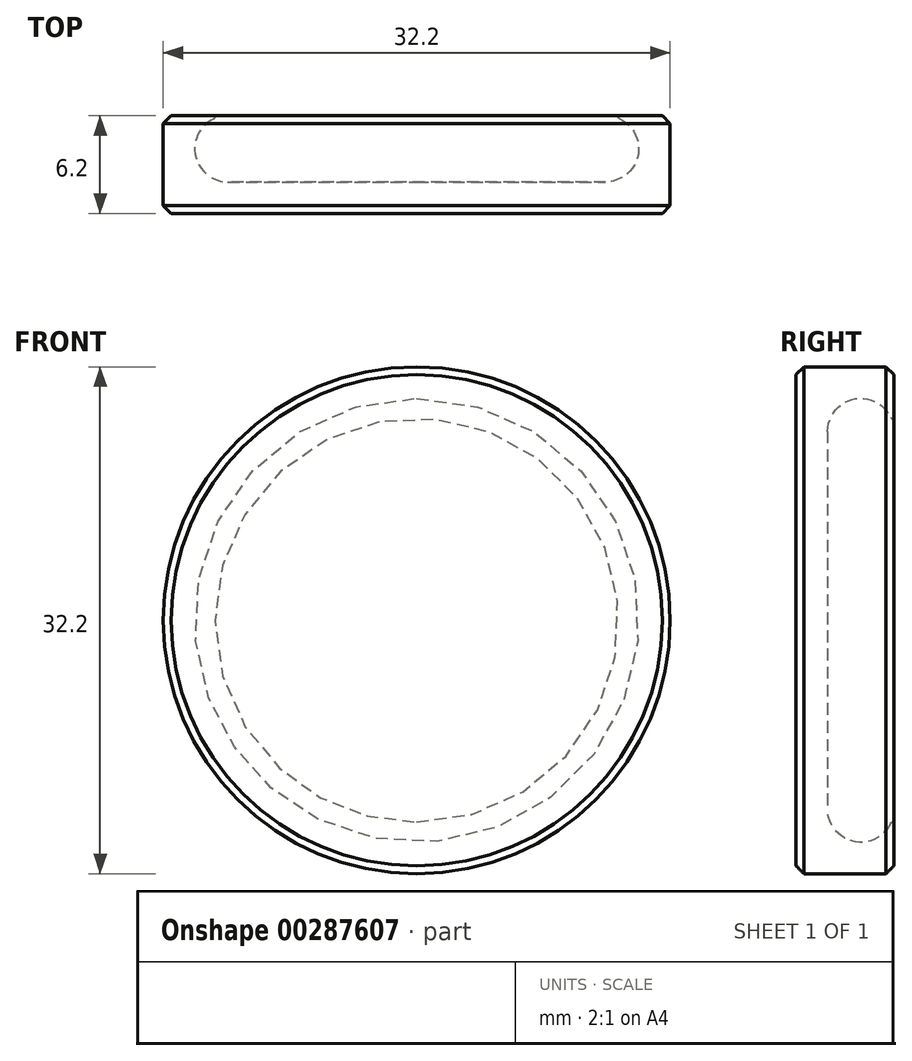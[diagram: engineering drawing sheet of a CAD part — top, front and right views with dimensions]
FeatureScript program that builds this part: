
annotation { "Feature Type Name" : "Feature", "Feature Type Description" : "" }
export const myFeature = defineFeature(function(context is Context, id is Id, definition is map)
    precondition{}
    {
        {
            var Q0;
            Q0=qCreatedBy(makeId("Top.planeOp"),FACE);
            var sketch = newSketch(context, id + "F0", { "sketchPlane" : qUnion([Q0])});
            skLineSegment(sketch, "E0", {"start": v(0, 0) * mm, "end": v(12, 0) * mm, "construction": true});
            skCircle(sketch, "E1", {"center": v(12, 0) * mm, "radius": 2.1 * mm});
            skLineSegment(sketch, "E2", {"start": v(12, -2.1) * mm, "end": v(0, -2.1) * mm});
            skLineSegment(sketch, "E3", {"start": v(14.1, 0) * mm, "end": v(14.1, 2.1) * mm});
            skLineSegment(sketch, "E4", {"start": v(14.1, 2.1) * mm, "end": v(12, 2.1) * mm});
            skLineSegment(sketch, "E5", {"start": v(12, -2.1) * mm, "end": v(16.1, -2.1) * mm});
            skLineSegment(sketch, "E6", {"start": v(16.1, -2.1) * mm, "end": v(16.1, 2.1) * mm});
            skLineSegment(sketch, "E7", {"start": v(16.1, 2.1) * mm, "end": v(14.1, 2.1) * mm});
            skLineSegment(sketch, "E8", {"start": v(16.1, -4.1) * mm, "end": v(0, -4.1) * mm});
            skLineSegment(sketch, "E9", {"start": v(16.1, -4.1) * mm, "end": v(16.1, -2.1) * mm});
            skLineSegment(sketch, "E10", {"start": v(0, -2.1) * mm, "end": v(0, -4.1) * mm});
            skSolve(sketch);
        }
        {
            var Q0;
            Q0=qCreatedBy(makeId("Right.planeOp"),FACE);
            var sketch = newSketch(context, id + "F1", { "sketchPlane" : qUnion([Q0])});
            skLineSegment(sketch, "E11", {"start": v(7.83, 0) * mm, "end": v(-14.6, 0) * mm, "construction": true});
            skSolve(sketch);
        }
        {
            var Q0;
            Q0=makeQuery(id+"F0.imprint","IMPRINT",FACE,{"disambiguationData":[TD([[makeQuery(id+"F0.imprint","IMPRINT",EDGE,{"derivedFrom":sQuery(id+"F0.wireOp",EDGE,"E2")}),1.0]])]});
            var Q1;
            {var subQ1=sQuery(id+"F0.wireOp",EDGE,"E3");Q1=makeQuery(id+"F0.imprint","IMPRINT",FACE,{"disambiguationData":[TD([[makeQuery(id+"F0.imprint","IMPRINT",EDGE,{"derivedFrom":subQ1}),-1.0]])]});}
            var Q2;
            {var subQ0=sQuery(id+"F0.wireOp",EDGE,"E3");Q2=makeQuery(id+"F0.imprint","IMPRINT",FACE,{"disambiguationData":[TD([[makeQuery(id+"F0.imprint","IMPRINT",EDGE,{"derivedFrom":subQ0}),1.0]])]});}
            var Q3;
            Q3=sQuery(id+"F1.wireOp",EDGE,"E11");
            revolve(context, id + "F2", {"surfaceOperationType" : NewSurfaceOperationType.NEW, "entities" : qUnion([Q0, Q1, Q2]), "axis" : qUnion([Q3]), "revolveType" : RevolveType.FULL});
        }
        {
            var Q0;
            Q0=makeQuery(id+"F2.opRevolve","SWEPT_EDGE",EDGE,{"disambiguationData":[OSD([sQuery(id+"F0.wireOp",EDGE,"E8"),sQuery(id+"F0.wireOp",EDGE,"E9")])]});
            var Q1;
            Q1=makeQuery(id+"F2.opRevolve","SWEPT_EDGE",EDGE,{"disambiguationData":[OSD([sQuery(id+"F0.wireOp",EDGE,"E6"),sQuery(id+"F0.wireOp",EDGE,"E7")])]});
            chamfer(context, id + "F3", {"entities" : qUnion([Q0, Q1]), "width" : 0.5 * mm, "tangentPropagation" : true});
        }
        {
            var Q0;
            Q0=makeQuery(id+"F2.opRevolve","SWEPT_EDGE",EDGE,{"disambiguationData":[OSD([sQuery(id+"F0.wireOp",EDGE,"E1"),sQuery(id+"F0.wireOp",EDGE,"E4")])]});
            fillet(context, id + "F4", {"entities" : qUnion([Q0]), "radius" : 0.1 * mm, "tangentPropagation" : true, "allowEdgeOverflow" : false});
        }
    });
